# Revit family: Gira_212800
name_source: partatom
category: Electrical Fixtures
revit_build: Autodesk Revit 2017 (Build: 20160225_1515(x64)
units: mm (PartAtom-declared; Revit-internal decimal feet)

## family parameters
Cut with Voids When Loaded = No
Host = Face
Maintain Annotation Orientation = No
Part Type = Normal
Room Calculation Point = No
Round Connector Dimension = Use Diameter
Shared = No

## types (1)
- Bin.input 8-g 12 - 48 V AC/DC zero-volt. KNX DRA
    BIM = https://media.live.bim.site 8f.rfa
    BIMSITE_PRODUCT_ID = 7bffefd257eabbc41457cb73de1d5ba235a54360
    Bus connection included = No
    Cost = 0 $
    Default Elevation = 1219 mm
    Description = Bin.in.8g 12-48V AC DC DRA KNX KNX binary input 8-gang 12 - 48 V AC DC zero-voltage,DRA plus DRA binary inputs for connecting contacts. The switching processes of contacts (e.g. sentinels buttons) are converted to KNX telegrams. The inputs can be assigned various functions or blocked independently of each other in the process. Signal display possible via yellow status LEDs.,Features: - Each input has full function. All channel-oriented functions can be parameterised separately per input. - Actively transmitting telegrams of inputs can be delayed globally based on bus voltage return or ETS programming. - Debounce and telegram rate limit are configurable. - Free assignment of the functions switching, dimming, blind, value transmitter and pulse counter to the inputs. - Blocker for blocking individual inputs (polarity of the blocking object adjustable) for the functions switching, dimming, blind and value transmitter. - Behaviour upon bus voltage recovery can be configured separately for each input. - Switching function: Two independent switching objects are available for each input (switching commands can be individually configured), command for leading and trailing edge can be set independently (ON, OFF, CHANGE, no reaction), independent cyclical transmission of the switching object depending on the edge or depending on the object value can be selected. - Dimming function: single and double-surface operation, time between dimming and switching and dim-step size can be set, telegram repetition and stop-telegram transmission possible. - Blind function: Command can be set with rising edge (no function, UP, DOWN, CHANGE), operating concept can be configured (Step - Move - Step or Move - Step), time between short and long-term operation can be set (only with Step - Move - Step), slat adjustment time can be set. - Value transmitter function: edge (button as NO contact, button as NC contact, switch) and value with edge can be configured, value adjustment with button by pressing and holding button for value transmitters possible, light scene auxiliary unit with memory function and saving of the scene without previously calling up is possible. - Pulse counter function: Counting interval is adjustable, edges (counting with leading edge, counting with trailing edge, counting with leading and trailing edge) are programmable, number of pulses required at the input can be configured, number of required counts for a counter change can be configured, each input includes a main counter and an intermediate counter, main counter and intermediate counter can operate separately from each other as a forward or reverse counter, start and end values of the counter can be set via parameter or communication object, count status can be read via KNX or automatically, performance after counter operation is programmable, reset pulse counter via KNX (counter reset). - The binary input has eight independent inputs in the voltage range of 12 to 48 V that are connected to the electrical signals. - Evaluation of direct current voltage signals (DC) or alternating current voltage signals (AC). - The binary input has a separate  24 V DC auxiliary voltage (SELV) available for connecting zero-voltage contacts. - Status message in case of error with the auxiliary voltage on the bus can be removed. - Possibility to connect meters with S0 interface (e.g. energy, gas, water meter).
    GTIN = 4010337018841
    HAN = 212800
    Handschaltung = No
    HeinzeBIM = https://www.heinze.de
    Input voltage [Volt] = [12:48]
    Local operation/hand operation = No
    Manufacturer = Gira
    Max. number of venetian-blind outputs = 0
    Number of binary inputs = 0
    Number of inputs = 8
    Number of outputs = 0
    Rated current [Ampere] = 0
    Stellgröße schaltend = No
    Stellgröße stetig = No
    Suitable for C-load = No
    Type of voltage (input voltage) = AC/DC
    URL = https://www.gira.de
    Ventilschutzfunktion = No
    With switch function = No

## geometry (parser evidence)
native form markers: Blend x2, Sweep x3
no freeform markers — native parametric forms only
